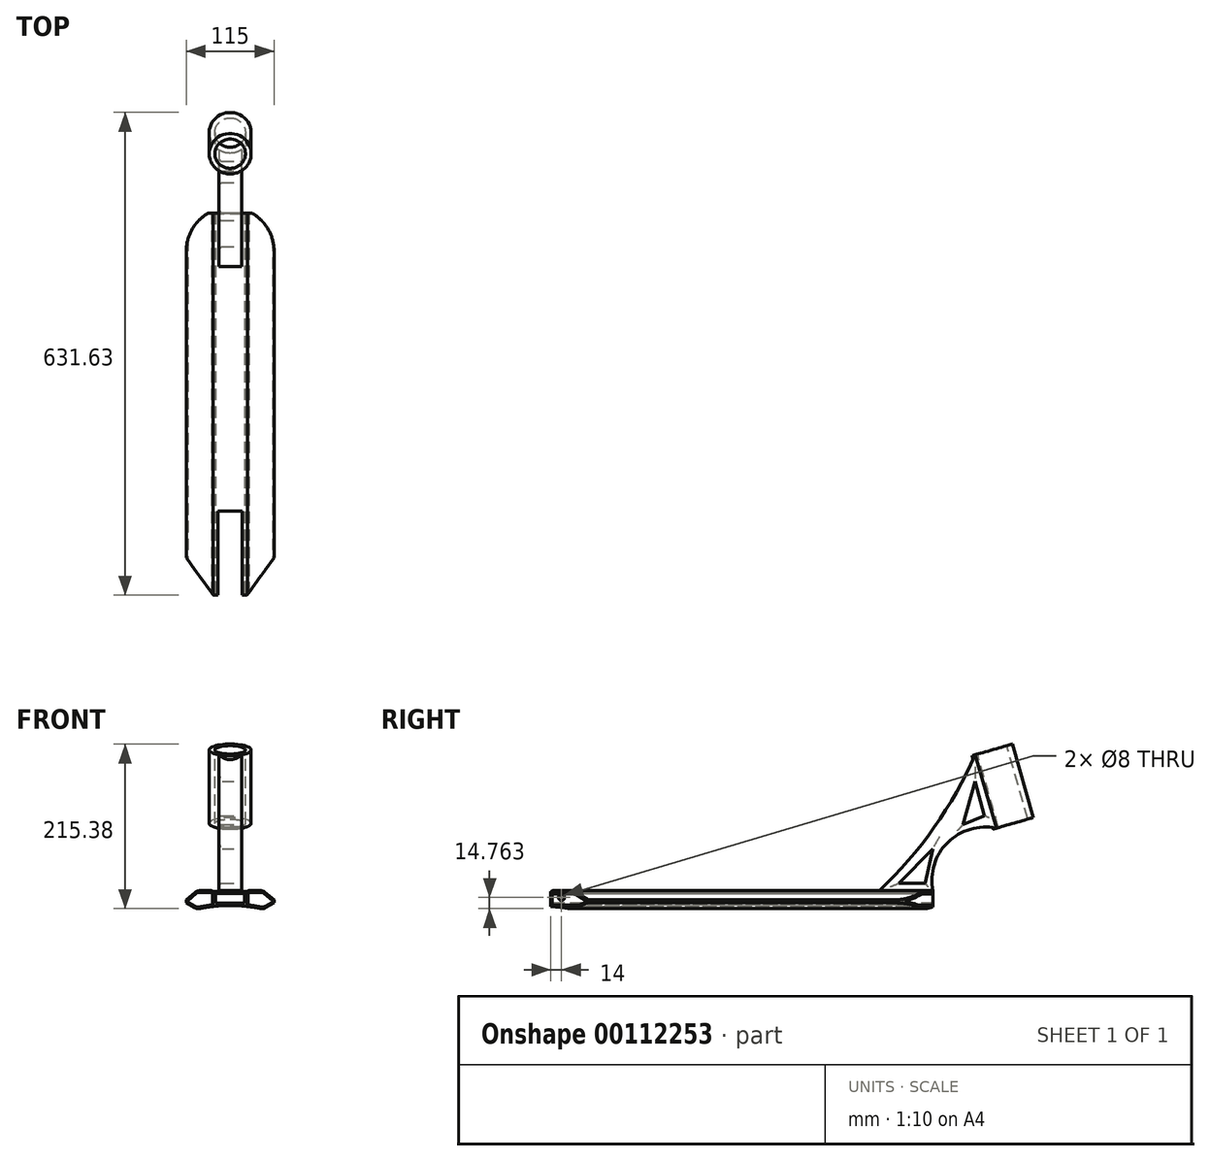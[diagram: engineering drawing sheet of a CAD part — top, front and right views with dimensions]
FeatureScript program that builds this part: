
annotation { "Feature Type Name" : "Feature", "Feature Type Description" : "" }
export const myFeature = defineFeature(function(context is Context, id is Id, definition is map)
    precondition{}
    {
        {
            var Q0;
            Q0=qCreatedBy(makeId("Front.planeOp"),FACE);
            var sketch = newSketch(context, id + "F0", { "sketchPlane" : qUnion([Q0])});
            skLineSegment(sketch, "E0", {"start": v(0, 0) * mm, "end": v(0, 76.05) * mm, "construction": true});
            skLineSegment(sketch, "E1", {"start": v(0, 21.21) * mm, "end": v(22.5, 21.21) * mm});
            skLineSegment(sketch, "E2", {"start": v(22.5, 21.21) * mm, "end": v(22.5, 22.51) * mm});
            skLineSegment(sketch, "E3", {"start": v(22.5, 22.51) * mm, "end": v(43.37, 22.51) * mm});
            skLineSegment(sketch, "E4", {"start": v(43.37, 22.51) * mm, "end": v(57.5, 10.66) * mm});
            skLineSegment(sketch, "E5", {"start": v(57.5, 10.66) * mm, "end": v(57.5, 6.66) * mm});
            skLineSegment(sketch, "E6", {"start": v(57.5, 6.66) * mm, "end": v(43.4, -1.49) * mm});
            skLineSegment(sketch, "E7.MirrorCS", {"start": v(-22.5, 22.51) * mm, "end": v(-43.37, 22.51) * mm});
            skLineSegment(sketch, "E8.MirrorCS", {"start": v(-22.5, 21.21) * mm, "end": v(-22.5, 22.51) * mm});
            skLineSegment(sketch, "E9.MirrorCS", {"start": v(0, 21.21) * mm, "end": v(-22.5, 21.21) * mm});
            skLineSegment(sketch, "E10.MirrorCS", {"start": v(-43.37, 22.51) * mm, "end": v(-57.5, 10.66) * mm});
            skLineSegment(sketch, "E11.MirrorCS", {"start": v(-57.5, 10.66) * mm, "end": v(-57.5, 6.66) * mm});
            skLineSegment(sketch, "E12.MirrorCS", {"start": v(-57.5, 6.66) * mm, "end": v(-43.4, -1.49) * mm});
            skArc(sketch, "E13", {"start": v(43.4, -1.49) * mm, "mid": v(0, 3.28) * mm, "end": v(-43.4, -1.49) * mm});
            skSolve(sketch);
        }
        {
            var Q0;
            Q0 = qSketchRegion(id + "F0", true);
            extrude(context, id + "F1", {"entities" : qUnion([Q0]), "endBound" : BoundingType.SYMMETRIC, "depth" : 500 * mm});
        }
        {
            var Q0;
            Q0=qCreatedBy(makeId("Front.planeOp"),FACE);
            var sketch = newSketch(context, id + "F2", { "sketchPlane" : qUnion([Q0])});
            skLineSegment(sketch, "E14", {"start": v(19, 6.21) * mm, "end": v(19, 19.21) * mm});
            skLineSegment(sketch, "E15", {"start": v(19, 19.21) * mm, "end": v(-19, 19.21) * mm});
            skLineSegment(sketch, "E16", {"start": v(-19, 19.21) * mm, "end": v(-19, 6.21) * mm});
            skLineSegment(sketch, "E17", {"start": v(-19, 6.21) * mm, "end": v(19, 6.21) * mm});
            skSolve(sketch);
        }
        {
            var Q0;
            Q0 = qSketchRegion(id + "F2", true);
            extrude(context, id + "F3", {"entities" : qUnion([Q0]), "operationType" : NewBodyOperationType.REMOVE, "endBound" : BoundingType.SYMMETRIC, "oppositeDirection" : true, "depth" : 500 * mm});
        }
        {
            var Q0;
            Q0=makeQuery(id+"F1.opExtrude","SWEPT_EDGE",EDGE,{"disambiguationData":[OSD([sQuery(id+"F0.wireOp",EDGE,"E7.MirrorCS"),sQuery(id+"F0.wireOp",EDGE,"E8.MirrorCS")])]});
            var Q1;
            Q1=makeQuery(id+"F1.opExtrude","SWEPT_EDGE",EDGE,{"disambiguationData":[OSD([sQuery(id+"F0.wireOp",EDGE,"E2"),sQuery(id+"F0.wireOp",EDGE,"E3")])]});
            fillet(context, id + "F4", {"entities" : qUnion([Q0, Q1]), "radius" : 2 * mm, "tangentPropagation" : true, "allowEdgeOverflow" : false});
        }
        {
            var Q0;
            Q0=makeQuery(id+"F1.opExtrude","SWEPT_EDGE",EDGE,{"disambiguationData":[OSD([sQuery(id+"F0.wireOp",EDGE,"E3"),sQuery(id+"F0.wireOp",EDGE,"E4")])]});
            var Q1;
            Q1=makeQuery(id+"F1.opExtrude","SWEPT_EDGE",EDGE,{"disambiguationData":[OSD([sQuery(id+"F0.wireOp",EDGE,"E6"),sQuery(id+"F0.wireOp",EDGE,"E13")])]});
            var Q2;
            Q2=makeQuery(id+"F1.opExtrude","SWEPT_EDGE",EDGE,{"disambiguationData":[OSD([sQuery(id+"F0.wireOp",EDGE,"E12.MirrorCS"),sQuery(id+"F0.wireOp",EDGE,"E13")])]});
            var Q3;
            Q3=makeQuery(id+"F1.opExtrude","SWEPT_EDGE",EDGE,{"disambiguationData":[OSD([sQuery(id+"F0.wireOp",EDGE,"E7.MirrorCS"),sQuery(id+"F0.wireOp",EDGE,"E10.MirrorCS")])]});
            fillet(context, id + "F5", {"entities" : qUnion([Q0, Q1, Q2, Q3]), "radius" : 9 * mm, "tangentPropagation" : true, "allowEdgeOverflow" : false});
        }
        {
            var Q0;
            Q0=makeQuery(id+"F1.opExtrude","CAP_FACE",FACE,{"disambiguationData":[OSD([sQuery(id+"F0.wireOp",EDGE,"E1"),sQuery(id+"F0.wireOp",EDGE,"E2"),sQuery(id+"F0.wireOp",EDGE,"E3"),sQuery(id+"F0.wireOp",EDGE,"E4"),sQuery(id+"F0.wireOp",EDGE,"E5"),sQuery(id+"F0.wireOp",EDGE,"E6"),sQuery(id+"F0.wireOp",EDGE,"E7.MirrorCS"),sQuery(id+"F0.wireOp",EDGE,"E8.MirrorCS"),sQuery(id+"F0.wireOp",EDGE,"E9.MirrorCS"),sQuery(id+"F0.wireOp",EDGE,"E10.MirrorCS"),sQuery(id+"F0.wireOp",EDGE,"E11.MirrorCS"),sQuery(id+"F0.wireOp",EDGE,"E12.MirrorCS"),sQuery(id+"F0.wireOp",EDGE,"E13")])],"isStart":false});
            var sketch = newSketch(context, id + "F6", { "sketchPlane" : qUnion([Q0])});
            skLineSegment(sketch, "E18.0.0", {"start": v(-24.37, 22.51) * mm, "end": v(-40.1, 22.51) * mm});
            skArc(sketch, "E18.0.1", {"start": v(-40.1, 22.51) * mm, "mid": v(-43.17, 21.97) * mm, "end": v(-45.88, 20.4) * mm});
            skLineSegment(sketch, "E18.0.2", {"start": v(-45.88, 20.4) * mm, "end": v(-57.5, 10.66) * mm});
            skLineSegment(sketch, "E18.0.3", {"start": v(-57.5, 10.66) * mm, "end": v(-57.5, 6.66) * mm});
            skLineSegment(sketch, "E18.0.4", {"start": v(-57.5, 6.66) * mm, "end": v(-46.4, 0.24) * mm});
            skArc(sketch, "E18.0.5", {"start": v(-46.4, 0.24) * mm, "mid": v(-43.33, -0.85) * mm, "end": v(-40.09, -0.78) * mm});
            skArc(sketch, "E18.0.6", {"start": v(-40.09, -0.78) * mm, "mid": v(0, 3.28) * mm, "end": v(40.09, -0.78) * mm});
            skArc(sketch, "E18.0.7", {"start": v(40.09, -0.78) * mm, "mid": v(43.33, -0.85) * mm, "end": v(46.4, 0.24) * mm});
            skLineSegment(sketch, "E18.0.8", {"start": v(46.4, 0.24) * mm, "end": v(57.5, 6.66) * mm});
            skLineSegment(sketch, "E18.0.9", {"start": v(57.5, 6.66) * mm, "end": v(57.5, 10.66) * mm});
            skLineSegment(sketch, "E18.0.10", {"start": v(57.5, 10.66) * mm, "end": v(45.88, 20.4) * mm});
            skArc(sketch, "E18.0.11", {"start": v(45.88, 20.4) * mm, "mid": v(43.17, 21.97) * mm, "end": v(40.1, 22.51) * mm});
            skLineSegment(sketch, "E18.0.12", {"start": v(40.1, 22.51) * mm, "end": v(24.37, 22.51) * mm});
            skArc(sketch, "E18.0.13", {"start": v(24.37, 22.51) * mm, "mid": v(23.23, 22.16) * mm, "end": v(22.5, 21.21) * mm});
            skLineSegment(sketch, "E18.0.14", {"start": v(22.5, 21.21) * mm, "end": v(-21, 21.21) * mm});
            skArc(sketch, "E18.0.15", {"start": v(-22.5, 21.21) * mm, "mid": v(-23.23, 22.16) * mm, "end": v(-24.37, 22.51) * mm});
            skLineSegment(sketch, "E19.0", {"start": v(40.1, 20.51) * mm, "end": v(24.37, 20.51) * mm});
            skArc(sketch, "E19.1", {"start": v(44.6, 18.88) * mm, "mid": v(42.49, 20.1) * mm, "end": v(40.1, 20.51) * mm});
            skLineSegment(sketch, "E19.2", {"start": v(55.5, 9.72) * mm, "end": v(44.6, 18.88) * mm});
            skLineSegment(sketch, "E19.3", {"start": v(-55.5, 9.72) * mm, "end": v(-55.5, 7.81) * mm});
            skLineSegment(sketch, "E19.4", {"start": v(-44.6, 18.88) * mm, "end": v(-55.5, 9.72) * mm});
            skArc(sketch, "E19.5", {"start": v(-40.1, 20.51) * mm, "mid": v(-42.49, 20.1) * mm, "end": v(-44.6, 18.88) * mm});
            skLineSegment(sketch, "E19.6", {"start": v(-24.37, 20.51) * mm, "end": v(-40.1, 20.51) * mm});
            skLineSegment(sketch, "E19.7", {"start": v(-55.5, 7.81) * mm, "end": v(-45.4, 1.98) * mm});
            skArc(sketch, "E19.8", {"start": v(-45.4, 1.98) * mm, "mid": v(-43.01, 1.13) * mm, "end": v(-40.49, 1.18) * mm});
            skArc(sketch, "E19.9", {"start": v(-40.49, 1.18) * mm, "mid": v(-32.46, 2.65) * mm, "end": v(-24.37, 3.8) * mm});
            skArc(sketch, "E19.10", {"start": v(40.49, 1.18) * mm, "mid": v(43.01, 1.13) * mm, "end": v(45.4, 1.98) * mm});
            skLineSegment(sketch, "E19.11", {"start": v(45.4, 1.98) * mm, "end": v(55.5, 7.81) * mm});
            skLineSegment(sketch, "E19.12", {"start": v(55.5, 7.81) * mm, "end": v(55.5, 9.72) * mm});
            skArc(sketch, "E20.trimOffspring", {"start": v(24.37, 3.8) * mm, "mid": v(32.46, 2.65) * mm, "end": v(40.49, 1.18) * mm});
            skPoint(sketch, "E21.orphan", {"position": v(-21, 21.21) * mm});
            skPoint(sketch, "E22.orphan", {"position": v(21, 21.21) * mm});
            skLineSegment(sketch, "E23", {"start": v(-24.37, 20.51) * mm, "end": v(-24.37, 18.61) * mm});
            skLineSegment(sketch, "E24", {"start": v(-24.37, 18.61) * mm, "end": v(-23.07, 18.61) * mm});
            skLineSegment(sketch, "E25", {"start": v(-23.07, 18.61) * mm, "end": v(-23.07, 3.8) * mm});
            skLineSegment(sketch, "E26", {"start": v(-23.07, 3.8) * mm, "end": v(-24.37, 3.8) * mm});
            skLineSegment(sketch, "E27", {"start": v(24.37, 20.51) * mm, "end": v(24.37, 18.61) * mm});
            skLineSegment(sketch, "E28", {"start": v(24.37, 18.61) * mm, "end": v(23.07, 18.61) * mm});
            skLineSegment(sketch, "E29", {"start": v(23.07, 18.61) * mm, "end": v(23.07, 3.8) * mm});
            skLineSegment(sketch, "E30", {"start": v(23.07, 3.8) * mm, "end": v(24.37, 3.8) * mm});
            skSolve(sketch);
        }
        {
            var Q0;
            Q0 = qSketchRegion(id + "F6", true);
            extrude(context, id + "F7", {"entities" : qUnion([Q0]), "operationType" : NewBodyOperationType.REMOVE, "endBound" : BoundingType.THROUGH_ALL, "oppositeDirection" : true, "depth" : 25 * mm});
        }
        {
            var Q0;
            Q0=qCreatedBy(makeId("Top.planeOp"),FACE);
            var sketch = newSketch(context, id + "F8", { "sketchPlane" : qUnion([Q0])});
            skArc(sketch, "E31", {"start": v(57.5, 200) * mm, "mid": v(0, 257.5) * mm, "end": v(-57.5, 200) * mm});
            skLineSegment(sketch, "E32", {"start": v(-57.5, 200) * mm, "end": v(-57.5, 280) * mm});
            skLineSegment(sketch, "E33", {"start": v(57.5, 200) * mm, "end": v(57.5, 280) * mm});
            skLineSegment(sketch, "E34", {"start": v(57.5, 280) * mm, "end": v(-57.5, 280) * mm});
            skSolve(sketch);
        }
        {
            var Q0;
            Q0 = qSketchRegion(id + "F8", true);
            extrude(context, id + "F9", {"entities" : qUnion([Q0]), "operationType" : NewBodyOperationType.REMOVE, "depth" : 25 * mm, "hasSecondDirection" : true, "secondDirectionOppositeDirection" : true, "secondDirectionDepth" : 25 * mm});
        }
        {
            var Q0;
            Q0=qCreatedBy(makeId("Top.planeOp"),FACE);
            var sketch = newSketch(context, id + "F10", { "sketchPlane" : qUnion([Q0])});
            skLineSegment(sketch, "E35", {"start": v(-68, -201.27) * mm, "end": v(-68, -255.27) * mm});
            skLineSegment(sketch, "E36", {"start": v(-68, -255.27) * mm, "end": v(-57.5, -255.27) * mm});
            skLineSegment(sketch, "E37", {"start": v(-57.5, -255.27) * mm, "end": v(-57.5, -301.27) * mm});
            skLineSegment(sketch, "E38", {"start": v(-57.5, -301.27) * mm, "end": v(57.5, -301.27) * mm});
            skLineSegment(sketch, "E39", {"start": v(57.5, -301.27) * mm, "end": v(57.5, -255.27) * mm});
            skLineSegment(sketch, "E40", {"start": v(57.5, -255.27) * mm, "end": v(68, -255.27) * mm});
            skLineSegment(sketch, "E41", {"start": v(68, -255.27) * mm, "end": v(68, -201.27) * mm});
            skLineSegment(sketch, "E42", {"start": v(68, -201.27) * mm, "end": v(57.5, -201.27) * mm});
            skLineSegment(sketch, "E43", {"start": v(57.5, -201.27) * mm, "end": v(22.1, -250) * mm});
            skLineSegment(sketch, "E44", {"start": v(-22.1, -250) * mm, "end": v(-57.5, -201.27) * mm});
            skLineSegment(sketch, "E45", {"start": v(-57.5, -201.27) * mm, "end": v(-68, -201.27) * mm});
            skLineSegment(sketch, "E46", {"start": v(22.1, -250) * mm, "end": v(16, -250) * mm});
            skLineSegment(sketch, "E47", {"start": v(16, -250) * mm, "end": v(16, -140) * mm});
            skLineSegment(sketch, "E48", {"start": v(16, -140) * mm, "end": v(-16, -140) * mm});
            skLineSegment(sketch, "E49", {"start": v(-16, -140) * mm, "end": v(-16, -250) * mm});
            skLineSegment(sketch, "E50", {"start": v(-16, -250) * mm, "end": v(-22.1, -250) * mm});
            skLineSegment(sketch, "E51", {"start": v(0, -140) * mm, "end": v(0, 0) * mm});
            skSolve(sketch);
        }
        {
            var Q0;
            Q0 = qSketchRegion(id + "F10", true);
            extrude(context, id + "F11", {"entities" : qUnion([Q0]), "operationType" : NewBodyOperationType.REMOVE, "endBound" : BoundingType.THROUGH_ALL, "depth" : 25 * mm, "hasSecondDirection" : true, "secondDirectionOppositeDirection" : true, "secondDirectionDepth" : 25 * mm});
        }
        {
            var Q0;
            Q0=qCreatedBy(makeId("Right.planeOp"),FACE);
            var sketch = newSketch(context, id + "F12", { "sketchPlane" : qUnion([Q0])});
            skPoint(sketch, "E52", {"position": v(250, 22.51) * mm});
            skArc(sketch, "E53", {"start": v(180.01, 22.51) * mm, "mid": v(251.68, 105.23) * mm, "end": v(305.56, 200.5) * mm});
            skLineSegment(sketch, "E54", {"start": v(305.56, 200.5) * mm, "end": v(349.77, 213.19) * mm});
            skArc(sketch, "E55", {"start": v(333.12, 104.38) * mm, "mid": v(269.6, 85.75) * mm, "end": v(250, 22.51) * mm});
            skPoint(sketch, "E56", {"position": v(180.01, 0) * mm});
            skPoint(sketch, "E57", {"position": v(320.01, 22.51) * mm});
            skLineSegment(sketch, "E58", {"start": v(349.77, 213.19) * mm, "end": v(377.34, 117.06) * mm});
            skLineSegment(sketch, "E59", {"start": v(377.34, 117.06) * mm, "end": v(333.12, 104.38) * mm});
            skLineSegment(sketch, "E60", {"start": v(250, 22.51) * mm, "end": v(250, 21.22) * mm});
            skLineSegment(sketch, "E61", {"start": v(250, 21.22) * mm, "end": v(180.01, 21.22) * mm});
            skLineSegment(sketch, "E62", {"start": v(180.01, 21.22) * mm, "end": v(180.01, 22.51) * mm});
            skSolve(sketch);
        }
        {
            var Q0;
            Q0 = qSketchRegion(id + "F12", true);
            extrude(context, id + "F13", {"entities" : qUnion([Q0]), "operationType" : NewBodyOperationType.ADD, "endBound" : BoundingType.SYMMETRIC, "depth" : 30 * mm});
        }
        {
            var Q0;
            Q0=makeQuery(id+"F13.opExtrude","SWEPT_FACE",FACE,{"disambiguationData":[OSD([sQuery(id+"F12.wireOp",EDGE,"E54")])]});
            var sketch = newSketch(context, id + "F14", { "sketchPlane" : qUnion([Q0])});
            skSolve(sketch);
        }
        {
            var Q0;
            {var subQ0=sQuery(id+"F12.wireOp",EDGE,"E54");Q0=makeQuery(id+"F14.imprint","IMPRINT",FACE,{"disambiguationData":[TD([[makeQuery(id+"F14.imprint","IMPRINT",EDGE,{"derivedFrom":makeQuery(id+"F13.opExtrude","CAP_EDGE",EDGE,{"disambiguationData":[OSD([subQ0])],"isStart":true})}),-1.0]])]});}
            var sketch = newSketch(context, id + "F15", { "sketchPlane" : qUnion([Q0])});
            skCircle(sketch, "E63", {"center": v(0, 371.99) * mm, "radius": 27.46 * mm});
            skSolve(sketch);
        }
        {
            var Q0;
            Q0 = qSketchRegion(id + "F15", true);
            extrude(context, id + "F16", {"entities" : qUnion([Q0]), "operationType" : NewBodyOperationType.ADD, "oppositeDirection" : true, "depth" : 100 * mm});
        }
        {
            var Q0;
            Q0=makeQuery(id+"F16.boolean.opBoolean","MERGE",FACE,{"derivedFrom":[makeQuery(id+"F13.opExtrude","SWEPT_FACE",FACE,{"disambiguationData":[OSD([sQuery(id+"F12.wireOp",EDGE,"E54")])]}),makeQuery(id+"F16.opExtrude","CAP_FACE",FACE,{"disambiguationData":[OSD([sQuery(id+"F15.wireOp",EDGE,"E63")])],"isStart":true})]});
            var sketch = newSketch(context, id + "F17", { "sketchPlane" : qUnion([Q0])});
            skPoint(sketch, "E64", {"position": v(0, 371.99) * mm});
            skSolve(sketch);
        }
        {
            var Q0;
            Q0=sQuery(id+"F17.wireOp",VERTEX,"E64");
            var Q1;
            Q1=makeQuery(id+"F13.opExtrude","SWEPT_BODY",BODY,{"disambiguationData":[OSD([sQuery(id+"F12.wireOp",EDGE,"lBjGuwqI-sWZi-qE8o-DAsl-QYGnW6gCz3hu"),sQuery(id+"F12.wireOp",EDGE,"E53"),sQuery(id+"F12.wireOp",EDGE,"E54"),sQuery(id+"F12.wireOp",EDGE,"E55"),sQuery(id+"F12.wireOp",EDGE,"E58"),sQuery(id+"F12.wireOp",EDGE,"E59")])]});
            hole(context, id + "F18", {"style" : HoleStyle.SIMPLE, "endStyle" : HoleEndStyle.THROUGH, "holeDiameter" : 40 * mm, "locations" : qUnion([Q0]), "scope" : qUnion([Q1]), "isTappedThrough" : true});
        }
        {
            var Q0;
            Q0=makeQuery(id+"F7.boolean.opBoolean","COPY",FACE,{"derivedFrom":makeQuery(id+"F7.opExtrude","SWEPT_FACE",FACE,{"disambiguationData":[OSD([sQuery(id+"F6.wireOp",EDGE,"E29")])]})});
            var sketch = newSketch(context, id + "F19", { "sketchPlane" : qUnion([Q0])});
            skPoint(sketch, "E65", {"position": v(-236, 13.8) * mm});
            skSolve(sketch);
        }
        {
            var Q0;
            Q0=sQuery(id+"F19.wireOp",VERTEX,"E65");
            var Q1;
            Q1=makeQuery(id+"F1.opExtrude","SWEPT_BODY",BODY,{"disambiguationData":[OSD([sQuery(id+"F0.wireOp",EDGE,"E1"),sQuery(id+"F0.wireOp",EDGE,"E2"),sQuery(id+"F0.wireOp",EDGE,"E3"),sQuery(id+"F0.wireOp",EDGE,"E4"),sQuery(id+"F0.wireOp",EDGE,"E5"),sQuery(id+"F0.wireOp",EDGE,"E6"),sQuery(id+"F0.wireOp",EDGE,"E7.MirrorCS"),sQuery(id+"F0.wireOp",EDGE,"E8.MirrorCS"),sQuery(id+"F0.wireOp",EDGE,"E9.MirrorCS"),sQuery(id+"F0.wireOp",EDGE,"E10.MirrorCS"),sQuery(id+"F0.wireOp",EDGE,"E11.MirrorCS"),sQuery(id+"F0.wireOp",EDGE,"E12.MirrorCS"),sQuery(id+"F0.wireOp",EDGE,"E13")])]});
            hole(context, id + "F20", {"style" : HoleStyle.SIMPLE, "endStyle" : HoleEndStyle.THROUGH, "holeDiameter" : 8 * mm, "locations" : qUnion([Q0]), "scope" : qUnion([Q1]), "isTappedThrough" : true});
        }
        {
            var Q0;
            Q0=makeQuery(id+"F13.opExtrude","CAP_FACE",FACE,{"disambiguationData":[OSD([sQuery(id+"F12.wireOp",EDGE,"lBjGuwqI-sWZi-qE8o-DAsl-QYGnW6gCz3hu"),sQuery(id+"F12.wireOp",EDGE,"E53"),sQuery(id+"F12.wireOp",EDGE,"E54"),sQuery(id+"F12.wireOp",EDGE,"E55"),sQuery(id+"F12.wireOp",EDGE,"E58"),sQuery(id+"F12.wireOp",EDGE,"E59")])],"isStart":false});
            var sketch = newSketch(context, id + "F21", { "sketchPlane" : qUnion([Q0])});
            skLineSegment(sketch, "E66", {"start": v(206, 32.51) * mm, "end": v(240, 32.51) * mm});
            skLineSegment(sketch, "E67", {"start": v(240, 32.51) * mm, "end": v(250, 77.51) * mm});
            skLineSegment(sketch, "E68", {"start": v(206, 32.51) * mm, "end": v(250, 77.51) * mm});
            skLineSegment(sketch, "E69", {"start": v(305.13, 165.72) * mm, "end": v(289.77, 109.34) * mm});
            skLineSegment(sketch, "E70", {"start": v(289.77, 109.34) * mm, "end": v(317.53, 120.72) * mm});
            skLineSegment(sketch, "E71", {"start": v(305.13, 165.72) * mm, "end": v(317.53, 120.72) * mm});
            skSolve(sketch);
        }
        {
            var Q0;
            Q0 = qSketchRegion(id + "F21", true);
            extrude(context, id + "F22", {"entities" : qUnion([Q0]), "operationType" : NewBodyOperationType.REMOVE, "endBound" : BoundingType.THROUGH_ALL, "oppositeDirection" : true, "depth" : 25 * mm});
        }
        {
            var Q0;
            Q0=makeQuery(id+"F22.boolean.opBoolean","COPY",EDGE,{"derivedFrom":makeQuery(id+"F22.opExtrude","CAP_EDGE",EDGE,{"disambiguationData":[OSD([sQuery(id+"F21.wireOp",EDGE,"E68")])],"isStart":true})});
            var Q1;
            Q1=makeQuery(id+"F22.boolean.opBoolean","COPY",EDGE,{"derivedFrom":makeQuery(id+"F22.opExtrude","CAP_EDGE",EDGE,{"disambiguationData":[OSD([sQuery(id+"F21.wireOp",EDGE,"E66")])],"isStart":true})});
            var Q2;
            Q2=makeQuery(id+"F22.boolean.opBoolean","COPY",EDGE,{"derivedFrom":makeQuery(id+"F22.opExtrude","CAP_EDGE",EDGE,{"disambiguationData":[OSD([sQuery(id+"F21.wireOp",EDGE,"E67")])],"isStart":true})});
            var Q3;
            Q3=makeQuery(id+"F22.boolean.opBoolean","COPY",EDGE,{"derivedFrom":makeQuery(id+"F22.opExtrude","CAP_EDGE",EDGE,{"disambiguationData":[OSD([sQuery(id+"F21.wireOp",EDGE,"E70")])],"isStart":true})});
            var Q4;
            Q4=makeQuery(id+"F22.boolean.opBoolean","COPY",EDGE,{"derivedFrom":makeQuery(id+"F22.opExtrude","CAP_EDGE",EDGE,{"disambiguationData":[OSD([sQuery(id+"F21.wireOp",EDGE,"E71")])],"isStart":true})});
            var Q5;
            Q5=makeQuery(id+"F22.boolean.opBoolean","COPY",EDGE,{"derivedFrom":makeQuery(id+"F22.opExtrude","CAP_EDGE",EDGE,{"disambiguationData":[OSD([sQuery(id+"F21.wireOp",EDGE,"E69")])],"isStart":true})});
            var Q6;
            Q6=makeQuery(id+"F22.boolean.opBoolean","INTERSECT",EDGE,{"derivedFrom":[makeQuery(id+"F13.opExtrude","CAP_FACE",FACE,{"disambiguationData":[OSD([sQuery(id+"F12.wireOp",EDGE,"lBjGuwqI-sWZi-qE8o-DAsl-QYGnW6gCz3hu"),sQuery(id+"F12.wireOp",EDGE,"E53"),sQuery(id+"F12.wireOp",EDGE,"E54"),sQuery(id+"F12.wireOp",EDGE,"E55"),sQuery(id+"F12.wireOp",EDGE,"E58"),sQuery(id+"F12.wireOp",EDGE,"E59")])],"isStart":true}),makeQuery(id+"F22.opExtrude","SWEPT_FACE",FACE,{"disambiguationData":[OSD([sQuery(id+"F21.wireOp",EDGE,"E71")])]})]});
            var Q7;
            Q7=makeQuery(id+"F22.boolean.opBoolean","INTERSECT",EDGE,{"derivedFrom":[makeQuery(id+"F13.opExtrude","CAP_FACE",FACE,{"disambiguationData":[OSD([sQuery(id+"F12.wireOp",EDGE,"lBjGuwqI-sWZi-qE8o-DAsl-QYGnW6gCz3hu"),sQuery(id+"F12.wireOp",EDGE,"E53"),sQuery(id+"F12.wireOp",EDGE,"E54"),sQuery(id+"F12.wireOp",EDGE,"E55"),sQuery(id+"F12.wireOp",EDGE,"E58"),sQuery(id+"F12.wireOp",EDGE,"E59")])],"isStart":true}),makeQuery(id+"F22.opExtrude","SWEPT_FACE",FACE,{"disambiguationData":[OSD([sQuery(id+"F21.wireOp",EDGE,"E70")])]})]});
            var Q8;
            Q8=makeQuery(id+"F22.boolean.opBoolean","INTERSECT",EDGE,{"derivedFrom":[makeQuery(id+"F13.opExtrude","CAP_FACE",FACE,{"disambiguationData":[OSD([sQuery(id+"F12.wireOp",EDGE,"lBjGuwqI-sWZi-qE8o-DAsl-QYGnW6gCz3hu"),sQuery(id+"F12.wireOp",EDGE,"E53"),sQuery(id+"F12.wireOp",EDGE,"E54"),sQuery(id+"F12.wireOp",EDGE,"E55"),sQuery(id+"F12.wireOp",EDGE,"E58"),sQuery(id+"F12.wireOp",EDGE,"E59")])],"isStart":true}),makeQuery(id+"F22.opExtrude","SWEPT_FACE",FACE,{"disambiguationData":[OSD([sQuery(id+"F21.wireOp",EDGE,"E69")])]})]});
            var Q9;
            Q9=makeQuery(id+"F22.boolean.opBoolean","INTERSECT",EDGE,{"derivedFrom":[makeQuery(id+"F13.opExtrude","CAP_FACE",FACE,{"disambiguationData":[OSD([sQuery(id+"F12.wireOp",EDGE,"lBjGuwqI-sWZi-qE8o-DAsl-QYGnW6gCz3hu"),sQuery(id+"F12.wireOp",EDGE,"E53"),sQuery(id+"F12.wireOp",EDGE,"E54"),sQuery(id+"F12.wireOp",EDGE,"E55"),sQuery(id+"F12.wireOp",EDGE,"E58"),sQuery(id+"F12.wireOp",EDGE,"E59")])],"isStart":true}),makeQuery(id+"F22.opExtrude","SWEPT_FACE",FACE,{"disambiguationData":[OSD([sQuery(id+"F21.wireOp",EDGE,"E67")])]})]});
            var Q10;
            Q10=makeQuery(id+"F22.boolean.opBoolean","INTERSECT",EDGE,{"derivedFrom":[makeQuery(id+"F13.opExtrude","CAP_FACE",FACE,{"disambiguationData":[OSD([sQuery(id+"F12.wireOp",EDGE,"lBjGuwqI-sWZi-qE8o-DAsl-QYGnW6gCz3hu"),sQuery(id+"F12.wireOp",EDGE,"E53"),sQuery(id+"F12.wireOp",EDGE,"E54"),sQuery(id+"F12.wireOp",EDGE,"E55"),sQuery(id+"F12.wireOp",EDGE,"E58"),sQuery(id+"F12.wireOp",EDGE,"E59")])],"isStart":true}),makeQuery(id+"F22.opExtrude","SWEPT_FACE",FACE,{"disambiguationData":[OSD([sQuery(id+"F21.wireOp",EDGE,"E68")])]})]});
            var Q11;
            Q11=makeQuery(id+"F22.boolean.opBoolean","INTERSECT",EDGE,{"derivedFrom":[makeQuery(id+"F13.opExtrude","CAP_FACE",FACE,{"disambiguationData":[OSD([sQuery(id+"F12.wireOp",EDGE,"lBjGuwqI-sWZi-qE8o-DAsl-QYGnW6gCz3hu"),sQuery(id+"F12.wireOp",EDGE,"E53"),sQuery(id+"F12.wireOp",EDGE,"E54"),sQuery(id+"F12.wireOp",EDGE,"E55"),sQuery(id+"F12.wireOp",EDGE,"E58"),sQuery(id+"F12.wireOp",EDGE,"E59")])],"isStart":true}),makeQuery(id+"F22.opExtrude","SWEPT_FACE",FACE,{"disambiguationData":[OSD([sQuery(id+"F21.wireOp",EDGE,"E66")])]})]});
            fillet(context, id + "F23", {"entities" : qUnion([Q0, Q1, Q2, Q3, Q4, Q5, Q6, Q7, Q8, Q9, Q10, Q11]), "radius" : 5 * mm, "tangentPropagation" : true, "allowEdgeOverflow" : false});
        }
    });
